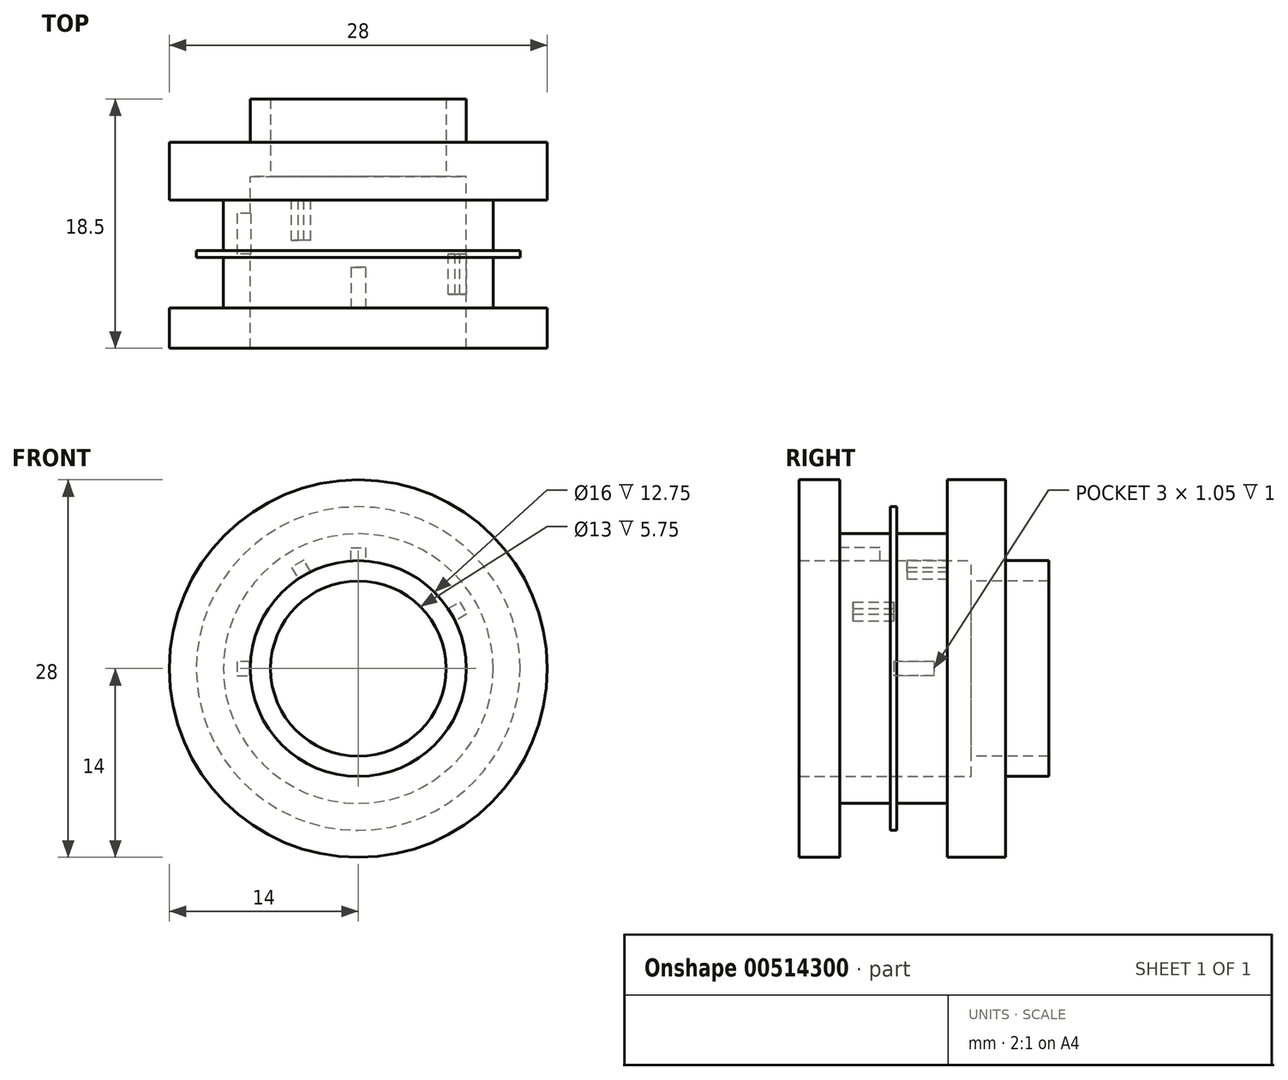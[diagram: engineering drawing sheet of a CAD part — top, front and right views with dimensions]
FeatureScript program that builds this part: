
annotation { "Feature Type Name" : "Feature", "Feature Type Description" : "" }
export const myFeature = defineFeature(function(context is Context, id is Id, definition is map)
    precondition{}
    {
        {
            var Q0;
            Q0=qCreatedBy(makeId("Front.planeOp"),FACE);
            var sketch = newSketch(context, id + "F0", { "sketchPlane" : qUnion([Q0])});
            skCircle(sketch, "E0", {"center": v(0, 0) * mm, "radius": 10 * mm});
            skCircle(sketch, "E1", {"center": v(0, 0) * mm, "radius": 8 * mm});
            skSolve(sketch);
        }
        {
            var Q0;
            Q0=makeQuery(id+"F0.imprint","IMPRINT",FACE,{"disambiguationData":[TD([[makeQuery(id+"F0.imprint","IMPRINT",EDGE,{"derivedFrom":sQuery(id+"F0.wireOp",EDGE,"E0")}),1.0]])]});
            extrude(context, id + "F1", {"entities" : qUnion([Q0]), "depth" : 8 * mm, "offsetDistance" : 25 * mm, "symmetric" : true});
        }
        {
            var Q0;
            Q0=makeQuery(id+"F1.opExtrude","CAP_FACE",FACE,{"disambiguationData":[OSD([sQuery(id+"F0.wireOp",EDGE,"E0"),sQuery(id+"F0.wireOp",EDGE,"E1")])],"isStart":false});
            var sketch = newSketch(context, id + "F2", { "sketchPlane" : qUnion([Q0])});
            skLineSegment(sketch, "E2", {"start": v(-0.53, 7.98) * mm, "end": v(-0.53, 8.98) * mm});
            skLineSegment(sketch, "E3", {"start": v(-0.53, 8.98) * mm, "end": v(0.53, 8.98) * mm});
            skLineSegment(sketch, "E4", {"start": v(0.52, 8.98) * mm, "end": v(0.53, 7.98) * mm});
            skSolve(sketch);
        }
        {
            var Q0;
            {var subQ0=sQuery(id+"F2.wireOp",EDGE,"E2");Q0=makeQuery(id+"F2.imprint","IMPRINT",FACE,{"disambiguationData":[TD([[makeQuery(id+"F2.imprint","IMPRINT",EDGE,{"derivedFrom":subQ0}),-1.0]])]});}
            extrude(context, id + "F3", {"entities" : qUnion([Q0]), "operationType" : NewBodyOperationType.REMOVE, "oppositeDirection" : true, "depth" : 3 * mm, "offsetDistance" : 25 * mm});
        }
        {
            var Q0;
            Q0=qCreatedBy(makeId("Front.planeOp"),FACE);
            var sketch = newSketch(context, id + "F4", { "sketchPlane" : qUnion([Q0])});
            skLineSegment(sketch, "E5", {"start": v(0, 0) * mm, "end": v(14.59, 8.42) * mm, "construction": true});
            skArc(sketch, "E6", {"start": v(7.18, 3.54) * mm, "mid": v(6.93, 4) * mm, "end": v(6.65, 4.45) * mm});
            skLineSegment(sketch, "E7", {"start": v(6.65, 4.45) * mm, "end": v(7.52, 4.95) * mm});
            skLineSegment(sketch, "E8", {"start": v(7.52, 4.95) * mm, "end": v(8.04, 4.04) * mm});
            skLineSegment(sketch, "E9", {"start": v(8.04, 4.04) * mm, "end": v(7.18, 3.54) * mm});
            skSolve(sketch);
        }
        {
            var Q0;
            Q0 = qSketchRegion(id + "F4", true);
            extrude(context, id + "F5", {"entities" : qUnion([Q0]), "operationType" : NewBodyOperationType.REMOVE, "depth" : 3 * mm, "offsetDistance" : 25 * mm});
        }
        {
            var Q0;
            Q0=makeQuery(id+"F1.opExtrude","CAP_FACE",FACE,{"disambiguationData":[OSD([sQuery(id+"F0.wireOp",EDGE,"E0"),sQuery(id+"F0.wireOp",EDGE,"E1")])],"isStart":true});
            var sketch = newSketch(context, id + "F6", { "sketchPlane" : qUnion([Q0])});
            skLineSegment(sketch, "E10", {"start": v(0, 0) * mm, "end": v(6.95, 12.04) * mm, "construction": true});
            skArc(sketch, "E11", {"start": v(4.45, 6.65) * mm, "mid": v(4, 6.93) * mm, "end": v(3.54, 7.18) * mm});
            skLineSegment(sketch, "E12", {"start": v(3.54, 7.18) * mm, "end": v(4.04, 8.04) * mm});
            skLineSegment(sketch, "E13", {"start": v(4.04, 8.04) * mm, "end": v(4.95, 7.52) * mm});
            skLineSegment(sketch, "E14", {"start": v(4.95, 7.52) * mm, "end": v(4.45, 6.65) * mm});
            skSolve(sketch);
        }
        {
            var Q0;
            Q0 = qSketchRegion(id + "F6", true);
            extrude(context, id + "F7", {"entities" : qUnion([Q0]), "operationType" : NewBodyOperationType.REMOVE, "oppositeDirection" : true, "depth" : 3 * mm, "offsetDistance" : 25 * mm});
        }
        {
            var Q0;
            Q0=qCreatedBy(makeId("Front.planeOp"),FACE);
            var sketch = newSketch(context, id + "F8", { "sketchPlane" : qUnion([Q0])});
            skLineSegment(sketch, "E15", {"start": v(0, 0) * mm, "end": v(-25.45, 0) * mm, "construction": true});
            skArc(sketch, "E16", {"start": v(-7.98, 0.52) * mm, "mid": v(-8, 0) * mm, "end": v(-7.98, -0.52) * mm});
            skLineSegment(sketch, "E17", {"start": v(-7.98, 0.52) * mm, "end": v(-8.98, 0.52) * mm});
            skLineSegment(sketch, "E18", {"start": v(-8.98, 0.52) * mm, "end": v(-8.98, -0.52) * mm});
            skLineSegment(sketch, "E19", {"start": v(-8.98, -0.53) * mm, "end": v(-7.98, -0.53) * mm});
            skSolve(sketch);
        }
        {
            var Q0;
            Q0 = qSketchRegion(id + "F8", true);
            var Q1;
            Q1 = qConstructionFilter(qBodyType(qCreatedBy(id + "F8" ,EDGE), BodyType.WIRE), ConstructionObject.NO);
            extrude(context, id + "F9", {"entities" : qUnion([Q0]), "operationType" : NewBodyOperationType.REMOVE, "surfaceEntities" : qUnion([Q1]), "oppositeDirection" : true, "depth" : 3 * mm, "offsetDistance" : 25 * mm});
        }
        {
            var Q0;
            Q0=qCreatedBy(makeId("Right.planeOp"),FACE);
            var sketch = newSketch(context, id + "F10", { "sketchPlane" : qUnion([Q0])});
            skLineSegment(sketch, "E20", {"start": v(4, 8) * mm, "end": v(4, 14) * mm});
            skLineSegment(sketch, "E21", {"start": v(4, 14) * mm, "end": v(8.3, 14) * mm});
            skLineSegment(sketch, "E22", {"start": v(8.3, 14) * mm, "end": v(8.3, 8) * mm});
            skLineSegment(sketch, "E23", {"start": v(8.3, 8) * mm, "end": v(11.5, 8) * mm});
            skLineSegment(sketch, "E24", {"start": v(11.5, 8) * mm, "end": v(11.5, 6.5) * mm});
            skLineSegment(sketch, "E25", {"start": v(11.5, 6.5) * mm, "end": v(5.75, 6.5) * mm});
            skLineSegment(sketch, "E26", {"start": v(5.75, 6.5) * mm, "end": v(5.75, 8) * mm});
            skLineSegment(sketch, "E27", {"start": v(5.75, 8) * mm, "end": v(4, 8) * mm});
            skLineSegment(sketch, "E28", {"start": v(-0.25, 10) * mm, "end": v(-0.25, 12) * mm});
            skLineSegment(sketch, "E29", {"start": v(-0.25, 12) * mm, "end": v(0.25, 12) * mm});
            skLineSegment(sketch, "E30", {"start": v(0.25, 12) * mm, "end": v(0.25, 10) * mm});
            skLineSegment(sketch, "E31", {"start": v(0.25, 10) * mm, "end": v(-0.25, 10) * mm});
            skLineSegment(sketch, "E32", {"start": v(-4, 8) * mm, "end": v(-4, 14) * mm});
            skLineSegment(sketch, "E33", {"start": v(-4, 14) * mm, "end": v(-7, 14) * mm});
            skLineSegment(sketch, "E34", {"start": v(-7, 14) * mm, "end": v(-7, 8) * mm});
            skLineSegment(sketch, "E35", {"start": v(-7, 8) * mm, "end": v(-4, 8) * mm});
            skSolve(sketch);
        }
        {
            var Q0;
            Q0 = qSketchRegion(id + "F10", true);
            var Q1;
            Q1=makeQuery(id+"F1.opExtrude","SWEPT_FACE",FACE,{"disambiguationData":[OSD([sQuery(id+"F0.wireOp",EDGE,"E0")])]});
            revolve(context, id + "F11", {"operationType" : NewBodyOperationType.ADD, "entities" : qUnion([Q0]), "axis" : qUnion([Q1]), "revolveType" : RevolveType.FULL});
        }
    });
